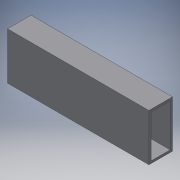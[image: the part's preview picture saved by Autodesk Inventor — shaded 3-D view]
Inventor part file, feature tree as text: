
AUTODESK INVENTOR PART (.ipt)
format: ipt  version: 2018 (Build 220112000, 112)  size: 134,144 bytes
history: native  units: in
note: dims shown in document units (in); Inventor stores cm internally (conversion verified against a paired STEP export)
features: extrude x2, sketch x2
ambient origin geometry x8: Origin, YZ Plane, XZ Plane, XY Plane, X Axis, Y Axis, Z Axis, Center Point
bodies: Solid1 (feature_tree)
feature tree (4):
  extrude  "Extrusion1"  Depth=2.0in
  extrude  "Extrusion2"  Depth=0.1in
  sketch  "Sketch1"  dims[d0=1.0in d1=2.0in]
  sketch  "Sketch2"  dims[d2=0.1in d3=0.1in d4=0.1in d5=0.1in d6=6.0in d7=0.0in d8=0.2031in d9=0.2031in d13=0.2031in d14=0.2031in d15=0.2031in d16=0.2031in d17=1.0in d18=0.5in d20=3.5in d21=0.5in d22=0.5in d23=2.5in d24=1.0in d25=0.5in d26=0.5in d27=0.5in d28=0.5in d29=0.5in d30=1.0in d31=0.0in]
